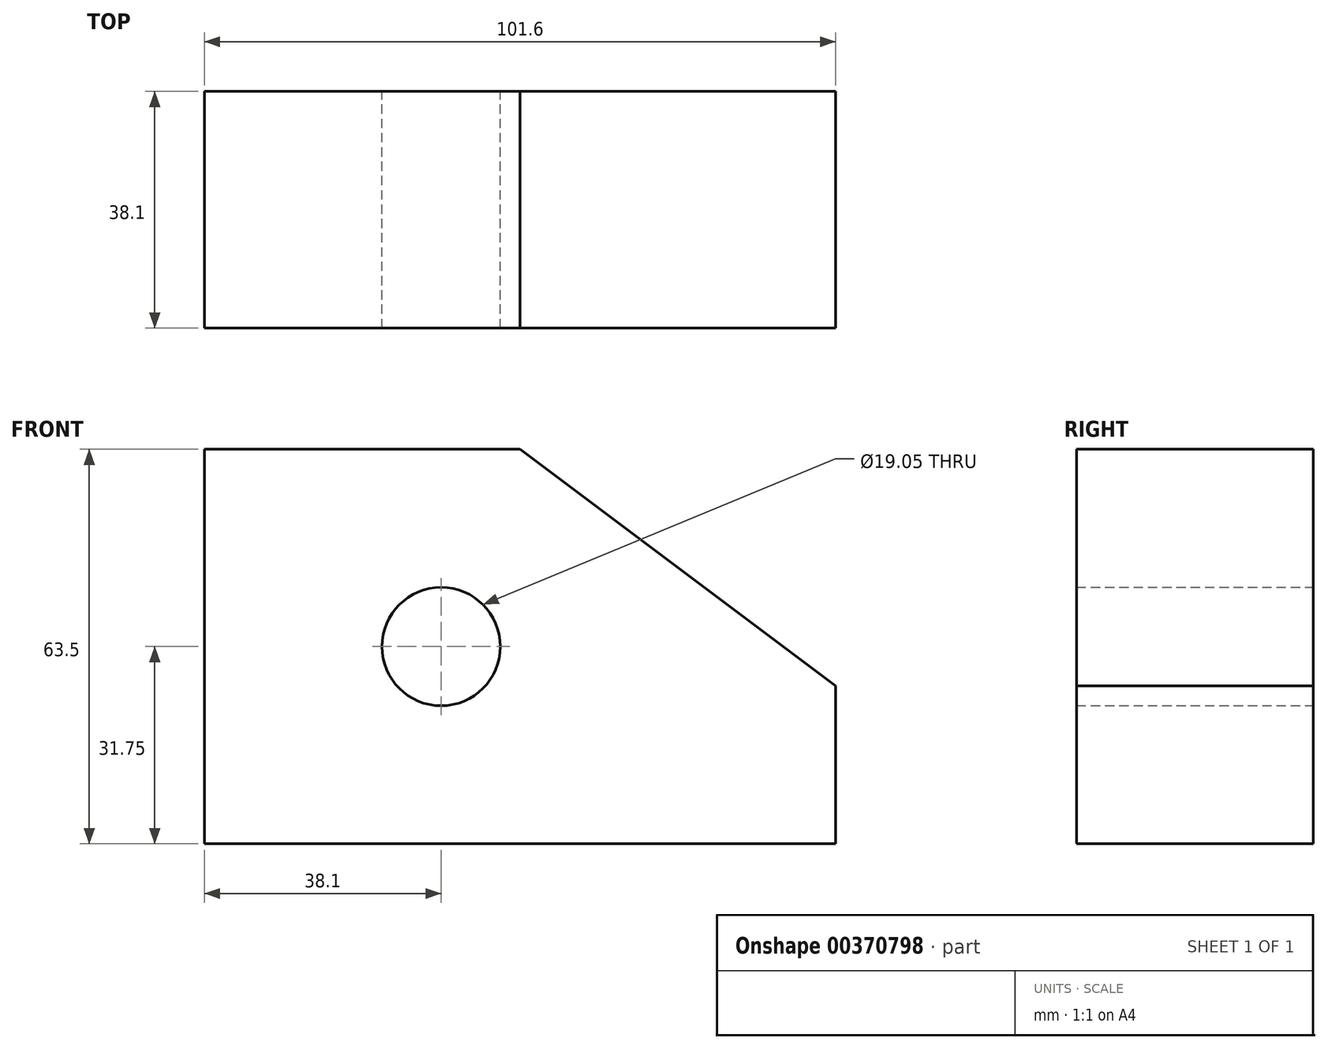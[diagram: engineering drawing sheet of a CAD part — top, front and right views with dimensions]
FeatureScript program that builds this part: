
annotation { "Feature Type Name" : "Feature", "Feature Type Description" : "" }
export const myFeature = defineFeature(function(context is Context, id is Id, definition is map)
    precondition{}
    {
        {
            var Q0;
            Q0=qCreatedBy(makeId("Front.planeOp"),FACE);
            var sketch = newSketch(context, id + "F0", { "sketchPlane" : qUnion([Q0])});
            skLineSegment(sketch, "E0", {"start": v(-38.1, 63.5) * mm, "end": v(12.7, 63.5) * mm});
            skLineSegment(sketch, "E1", {"start": v(-38.1, 63.5) * mm, "end": v(-38.1, 0) * mm});
            skLineSegment(sketch, "E2", {"start": v(-38.1, 0) * mm, "end": v(63.5, 0) * mm});
            skLineSegment(sketch, "E3", {"start": v(63.5, 0) * mm, "end": v(63.5, 25.4) * mm});
            skLineSegment(sketch, "E4", {"start": v(63.5, 25.4) * mm, "end": v(12.7, 63.5) * mm});
            skCircle(sketch, "E5", {"center": v(0, 31.75) * mm, "radius": 9.53 * mm});
            skSolve(sketch);
        }
        {
            var Q0;
            Q0=makeQuery(id+"F0.imprint","IMPRINT",FACE,{"disambiguationData":[TD([[makeQuery(id+"F0.imprint","IMPRINT",EDGE,{"derivedFrom":sQuery(id+"F0.wireOp",EDGE,"E0")}),-1.0]])]});
            extrude(context, id + "F1", {"entities" : qUnion([Q0]), "depth" : 38.1 * mm});
        }
    });
